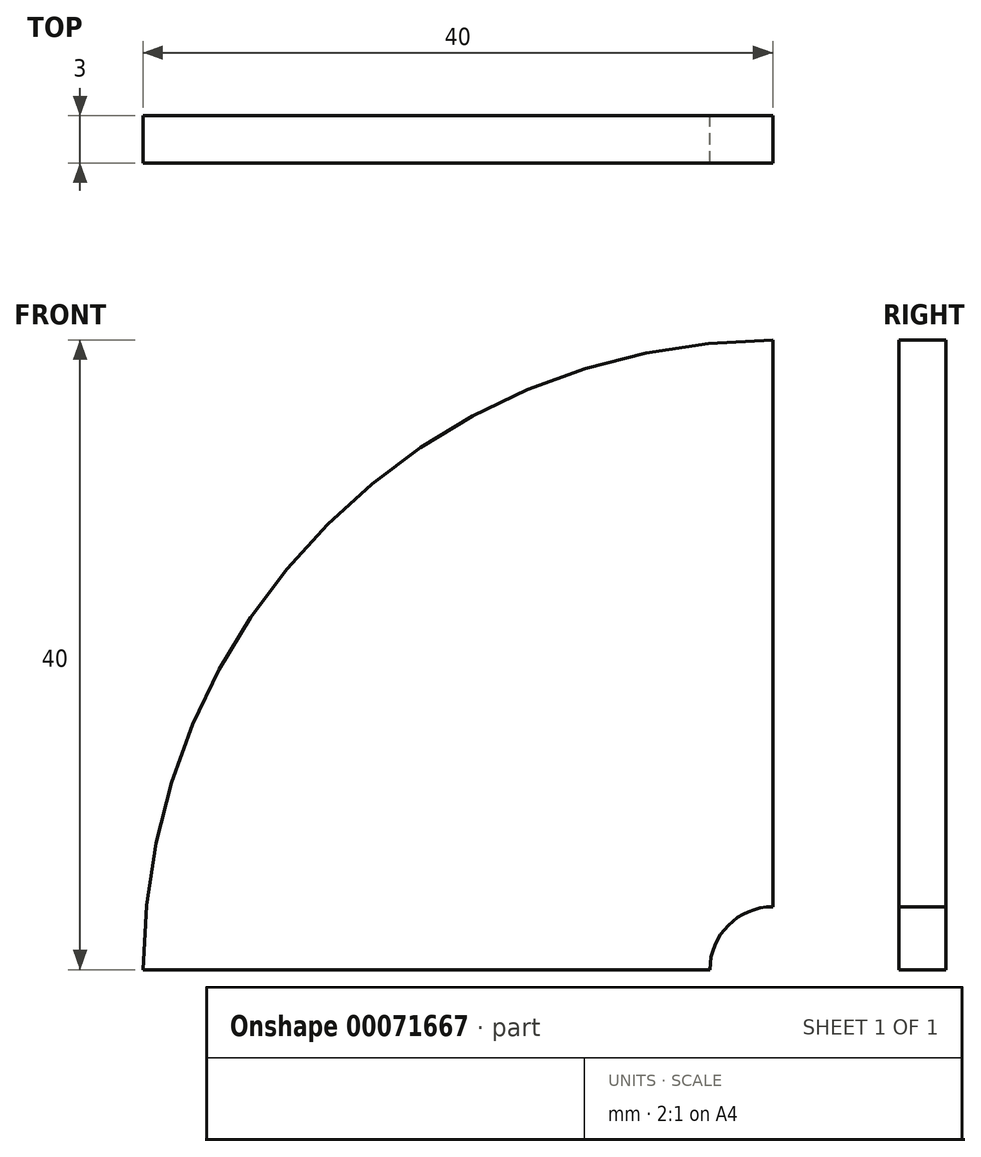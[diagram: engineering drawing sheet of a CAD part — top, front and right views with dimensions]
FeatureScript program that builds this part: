
annotation { "Feature Type Name" : "Feature", "Feature Type Description" : "" }
export const myFeature = defineFeature(function(context is Context, id is Id, definition is map)
    precondition{}
    {
        {
            var Q0;
            Q0=qCreatedBy(makeId("Front.planeOp"),FACE);
            var sketch = newSketch(context, id + "F0", { "sketchPlane" : qUnion([Q0])});
            skCircle(sketch, "E0", {"center": v(0, 0) * mm, "radius": 40 * mm});
            skCircle(sketch, "E1", {"center": v(0, 0) * mm, "radius": 4 * mm});
            skLineSegment(sketch, "E2", {"start": v(0, 40) * mm, "end": v(0, 4) * mm});
            skLineSegment(sketch, "E3", {"start": v(-4, 0) * mm, "end": v(-40, 0) * mm});
            skSolve(sketch);
        }
        {
            var Q0;
            {var subQ0=sQuery(id+"F0.wireOp",EDGE,"E2");Q0=makeQuery(id+"F0.imprint","IMPRINT",FACE,{"disambiguationData":[TD([[makeQuery(id+"F0.imprint","IMPRINT",EDGE,{"derivedFrom":subQ0}),-1.0]])]});}
            extrude(context, id + "F1", {"entities" : qUnion([Q0]), "depth" : 3 * mm});
        }
    });
